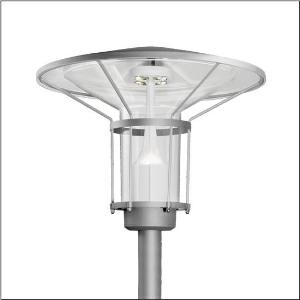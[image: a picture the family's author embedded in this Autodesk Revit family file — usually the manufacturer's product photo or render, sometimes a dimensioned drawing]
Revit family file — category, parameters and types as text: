
# Revit family: laterne_classic_iq___st1_2a_5xa5245ef14h_7fcb
name_source: partatom
category: Lighting Fixtures
units: mm (PartAtom-declared; Revit-internal decimal feet)

## family parameters
Cut with Voids When Loaded = No
Host = Face
Light Source = No
Part Type = Normal
Room Calculation Point = No
Round Connector Dimension = Use Diameter
Shared = No

## types (1)
- --- (1 x LED, 1380 lm, 10.5 W, 3000K)
    Apparent Load = 11 VA
    CIE Flux Codes = 21 60 93 97 100
    Color Rendering = 70
    Color Temperature = 3000K
    Default Elevation = 1800 mm
    Description = Lantern Classic iQ, mast luminaire, Module 540 iQ-SR, primary light control with 3 zone facetted reflector, of plastic, silver coated, highly specular, structured, primary optical cover: cover, of PMMA, transparent, light distribution: ST1.2a, light emission: direct distribution, primary light characteristic: asymmetric, installation type: post-top, LED, High Power LED, rated luminous flux: 1.380lm, luminous efficacy: 131lm/W, light colour: 730, colour temperature: 3000K, control gear: ECG iQ, control: Auto-Match, Temp-Guard, Lumen-Switch, Night-Set, Smart-Wire, Light-Fading, Desk-Remote (wireless, voltage-free reading and setting of iQ features in the workshop via application-optimized NFC function/RFID function), optimised constant luminous flux control (CLO 2.0), Street-Remote, pre-setting: logarithmic dimming characteristic, with terminal, 6-pole, max. 2.5mm², mains connection: 230..240V, AC, 50/60Hz, start of lifetime: 11W, end of service life: 11W, reduction: 5W, luminaire housing, upper part, of glass-fibre reinforced polyester, coated, Siteco® metallic grey (DB 702S), diameter: 750mm, height: 596mm, spigot size: d x l = 76 x 70mm (post-top) | with reducer (optional accessory) 60 x 70mm, post-top mast mounting element, of diecast aluminium, coated, Siteco® metallic grey (DB 702S), Module 540 iQ-SR, traffic white (RAL 9016), equipment: standard, protection rating (complete): IP65, insulation class (complete): insulation class II (safety insulation), certification: CE, ENEC, VDE, packaging unit: 1 piece

Light Distribution: ST1.2a
    Height = 596 mm
    Lamp = 1 x LED
    Lamp Light Flux = 1380 lm
    Lamp Power = 10.5 W
    Lamp count = 1
    Length = 750 mm
    Luminous efficacy = 131 lm/W
    Manufacturer = Siteco
    ModVariant = No
    Model = 5XA5245EF14H
    Number of Poles = 1
    OnlyDefault = Yes
    Power Factor = 1
    Product Name = Laterne Classic iQ | ST1.2a
    Product group = mast luminaire | pylon top
    ProductGroupID = 6100
    Protection Class = Protection class II
    Protection Degree = IP 65
    RLX_Detail_Level = 1
    RLX_Emergency_Light_Flux = 0 lm
    RLX_Emergency_Type = 0
    RLX_Emergency_Type_DB = No
    RlxData = <blob elided: 91245 chars, md5=db0bb9e7>
    Socket = socket
    Standby Power = 0 W
    System Light Flux = 1380 lm
    System Power = 11 W
    Type Comments = factory setting: luminous flux: 100 % | dim-lin: 254 | 419 mA
    Type Image = l_1006052.jpg
    URL = http://relux.com
    VarID = @adj_130733
    Voltage = 0 V
    Weight = 0.00 kg
    Width = 0 mm  [stored 0 ft]

note: [stored X ft] marks values corroborated as IEEE doubles in the binary element streams (Revit-internal decimal feet)

## geometry (parser evidence)
native form markers: Blend x4, Sweep x13
no freeform markers — native parametric forms only
